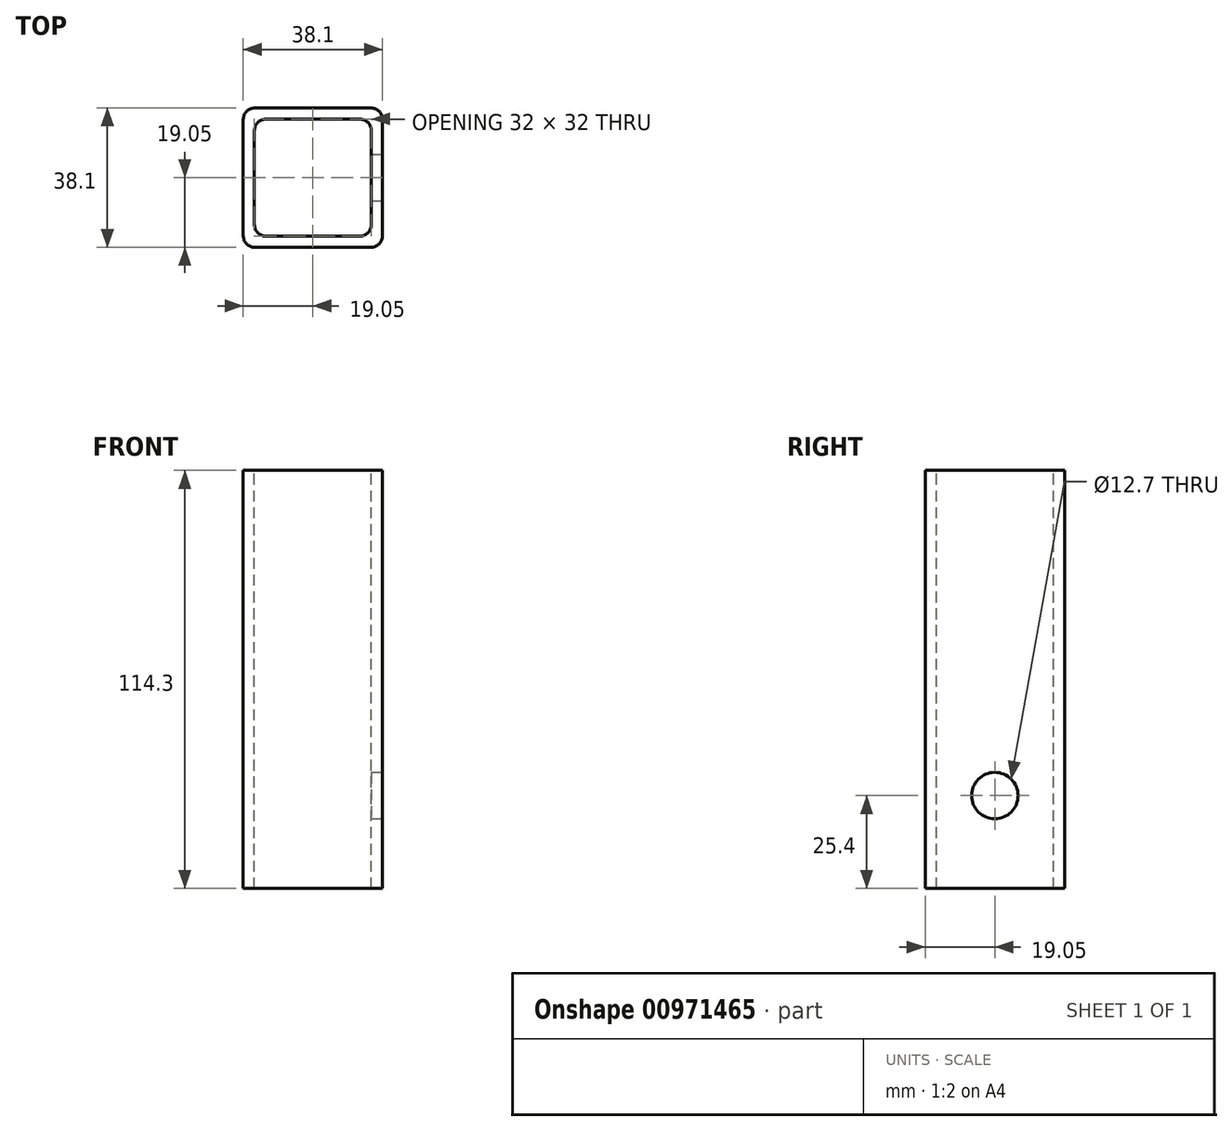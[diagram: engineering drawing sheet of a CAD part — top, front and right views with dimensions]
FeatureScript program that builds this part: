
annotation { "Feature Type Name" : "Feature", "Feature Type Description" : "" }
export const myFeature = defineFeature(function(context is Context, id is Id, definition is map)
    precondition{}
    {
        {
            var Q0;
            Q0=qCreatedBy(makeId("Top.planeOp"),FACE);
            var sketch = newSketch(context, id + "F0", { "sketchPlane" : qUnion([Q0])});
            skLineSegment(sketch, "E0.bottom", {"start": v(-15.87, 19.05) * mm, "end": v(15.88, 19.05) * mm});
            skLineSegment(sketch, "E0.top", {"start": v(-15.88, -19.05) * mm, "end": v(15.87, -19.05) * mm});
            skLineSegment(sketch, "E0.left", {"start": v(-19.05, 15.88) * mm, "end": v(-19.05, -15.88) * mm});
            skLineSegment(sketch, "E0.right", {"start": v(19.05, 15.88) * mm, "end": v(19.05, -15.88) * mm});
            skPoint(sketch, "E0.middle", {"position": v(0, 0) * mm});
            skLineSegment(sketch, "E1.0", {"start": v(-16, 12.83) * mm, "end": v(-16, -12.83) * mm});
            skLineSegment(sketch, "E1.1", {"start": v(-12.83, 16) * mm, "end": v(12.83, 16) * mm});
            skLineSegment(sketch, "E1.2", {"start": v(16, 12.83) * mm, "end": v(16, -12.83) * mm});
            skLineSegment(sketch, "E1.3", {"start": v(-12.83, -16) * mm, "end": v(12.83, -16) * mm});
            skPoint(sketch, "E2.visualSharp", {"position": v(-16, -16) * mm});
            skArc(sketch, "E2.filletArc", {"start": v(-16, -12.83) * mm, "mid": v(-15.07, -15.07) * mm, "end": v(-12.83, -16) * mm});
            skPoint(sketch, "E3.visualSharp", {"position": v(-16, 16) * mm});
            skArc(sketch, "E3.filletArc", {"start": v(-12.83, 16) * mm, "mid": v(-15.07, 15.07) * mm, "end": v(-16, 12.83) * mm});
            skPoint(sketch, "E4.visualSharp", {"position": v(16, 16) * mm});
            skArc(sketch, "E4.filletArc", {"start": v(16, 12.83) * mm, "mid": v(15.07, 15.07) * mm, "end": v(12.83, 16) * mm});
            skPoint(sketch, "E5.visualSharp", {"position": v(16, -16) * mm});
            skArc(sketch, "E5.filletArc", {"start": v(12.83, -16) * mm, "mid": v(15.07, -15.07) * mm, "end": v(16, -12.83) * mm});
            skPoint(sketch, "E6.visualSharp", {"position": v(19.05, -19.05) * mm});
            skArc(sketch, "E6.filletArc", {"start": v(15.87, -19.05) * mm, "mid": v(18.12, -18.12) * mm, "end": v(19.05, -15.88) * mm});
            skPoint(sketch, "E7.visualSharp", {"position": v(19.05, 19.05) * mm});
            skArc(sketch, "E7.filletArc", {"start": v(19.05, 15.88) * mm, "mid": v(18.12, 18.12) * mm, "end": v(15.88, 19.05) * mm});
            skPoint(sketch, "E8.visualSharp", {"position": v(-19.05, 19.05) * mm});
            skArc(sketch, "E8.filletArc", {"start": v(-15.87, 19.05) * mm, "mid": v(-18.12, 18.12) * mm, "end": v(-19.05, 15.88) * mm});
            skPoint(sketch, "E9.visualSharp", {"position": v(-19.05, -19.05) * mm});
            skArc(sketch, "E9.filletArc", {"start": v(-19.05, -15.88) * mm, "mid": v(-18.12, -18.12) * mm, "end": v(-15.88, -19.05) * mm});
            skSolve(sketch);
        }
        {
            var Q0;
            Q0 = qSketchRegion(id + "F0", true);
            extrude(context, id + "F1", {"entities" : qUnion([Q0]), "oppositeDirection" : true, "depth" : 114.3 * mm, "offsetDistance" : 25.4 * mm});
        }
        {
            var Q0;
            Q0=makeQuery(id+"F1.opExtrude","SWEPT_FACE",FACE,{"disambiguationData":[OSD([sQuery(id+"F0.wireOp",EDGE,"E0.right")])]});
            var sketch = newSketch(context, id + "F2", { "sketchPlane" : qUnion([Q0])});
            skCircle(sketch, "E10", {"center": v(0, -88.9) * mm, "radius": 6.35 * mm});
            skSolve(sketch);
        }
        {
            var Q0;
            Q0 = qSketchRegion(id + "F2", true);
            extrude(context, id + "F3", {"entities" : qUnion([Q0]), "operationType" : NewBodyOperationType.REMOVE, "oppositeDirection" : true, "depth" : 6.35 * mm, "offsetDistance" : 25.4 * mm});
        }
    });
